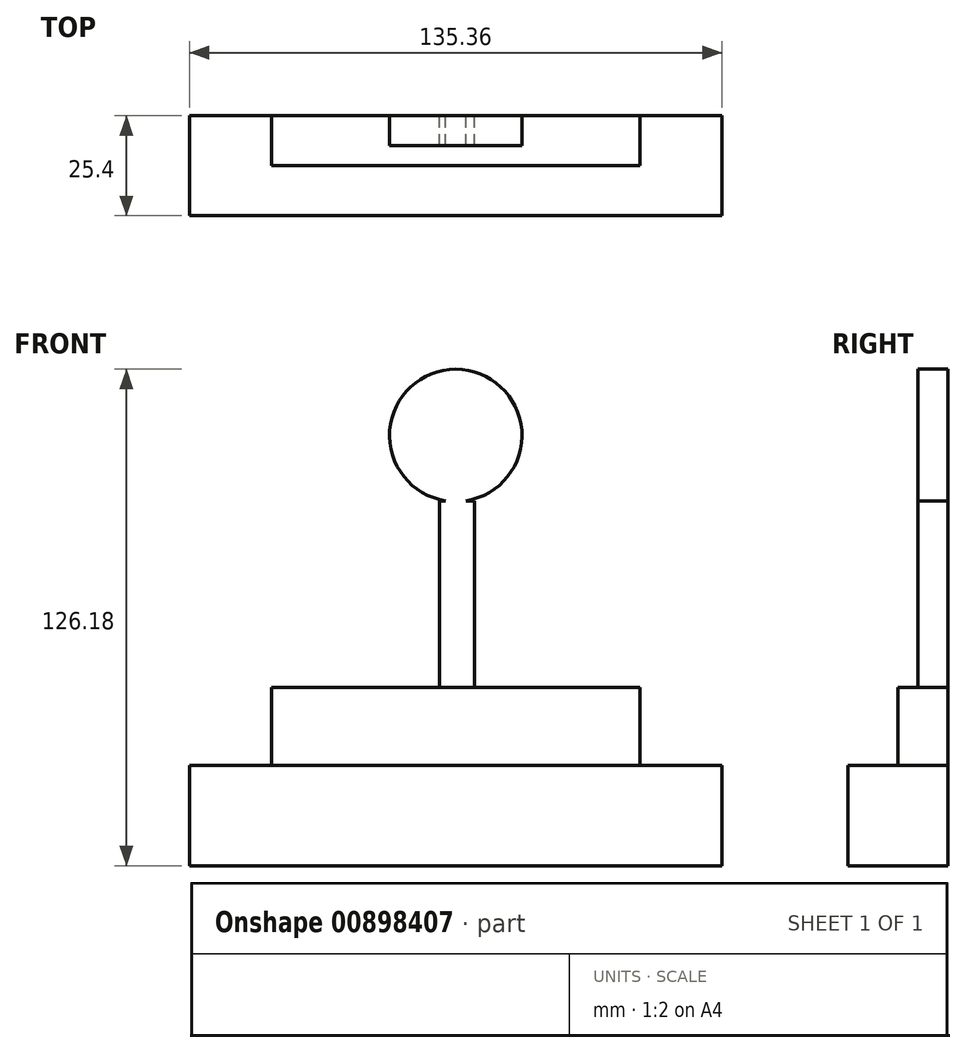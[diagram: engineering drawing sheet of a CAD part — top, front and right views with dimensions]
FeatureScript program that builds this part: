
annotation { "Feature Type Name" : "Feature", "Feature Type Description" : "" }
export const myFeature = defineFeature(function(context is Context, id is Id, definition is map)
    precondition{}
    {
        {
            var Q0;
            Q0=qCreatedBy(makeId("Front.planeOp"),FACE);
            var sketch = newSketch(context, id + "F0", { "sketchPlane" : qUnion([Q0])});
            skLineSegment(sketch, "E0.bottom", {"start": v(-67.68, -27.33) * mm, "end": v(67.68, -27.33) * mm});
            skLineSegment(sketch, "E0.top", {"start": v(-67.68, -52.83) * mm, "end": v(67.68, -52.83) * mm});
            skLineSegment(sketch, "E0.left", {"start": v(-67.68, -27.33) * mm, "end": v(-67.68, -52.83) * mm});
            skLineSegment(sketch, "E0.right", {"start": v(67.68, -27.33) * mm, "end": v(67.68, -52.83) * mm});
            skPoint(sketch, "E0.middle", {"position": v(0, -40.08) * mm});
            skLineSegment(sketch, "E1.bottom", {"start": v(-46.9, -7.35) * mm, "end": v(46.9, -7.35) * mm});
            skLineSegment(sketch, "E1.top", {"start": v(-46.9, -27.3) * mm, "end": v(46.9, -27.3) * mm});
            skLineSegment(sketch, "E1.left", {"start": v(-46.9, -7.35) * mm, "end": v(-46.9, -27.3) * mm});
            skLineSegment(sketch, "E1.right", {"start": v(46.9, -7.35) * mm, "end": v(46.9, -27.3) * mm});
            skPoint(sketch, "E1.middle", {"position": v(0, -17.33) * mm});
            skLineSegment(sketch, "E2.bottom", {"start": v(-5.61, 34.64) * mm, "end": v(4.92, 34.64) * mm});
            skLineSegment(sketch, "E2.top", {"start": v(-5.61, -7.35) * mm, "end": v(4.92, -7.35) * mm});
            skLineSegment(sketch, "E2.left", {"start": v(-5.61, 34.64) * mm, "end": v(-5.61, -7.35) * mm});
            skLineSegment(sketch, "E2.right", {"start": v(4.92, 34.64) * mm, "end": v(4.92, -7.35) * mm});
            skCircle(sketch, "E3", {"center": v(0, 53.45) * mm, "radius": 19.06 * mm});
            skLineSegment(sketch, "E4", {"start": v(0, 65.64) * mm, "end": v(-6.66, 55.94) * mm});
            skLineSegment(sketch, "E5", {"start": v(-6.66, 49) * mm, "end": v(-7.32, 41.58) * mm});
            skLineSegment(sketch, "E6", {"start": v(-7.32, 41.58) * mm, "end": v(0, 46.46) * mm});
            skLineSegment(sketch, "E7.MirrorCS", {"start": v(0, 65.64) * mm, "end": v(6.66, 55.94) * mm});
            skLineSegment(sketch, "E8.MirrorCS", {"start": v(7.32, 41.58) * mm, "end": v(0, 46.46) * mm});
            skLineSegment(sketch, "E9.MirrorCS", {"start": v(6.66, 49) * mm, "end": v(7.32, 41.58) * mm});
            skLineSegment(sketch, "E10", {"start": v(-6.66, 55.94) * mm, "end": v(-14.24, 55.94) * mm});
            skLineSegment(sketch, "E11", {"start": v(-14.24, 55.94) * mm, "end": v(-6.66, 49) * mm});
            skLineSegment(sketch, "E12", {"start": v(7.84, 55.94) * mm, "end": v(14.76, 55.94) * mm});
            skLineSegment(sketch, "E13", {"start": v(14.76, 55.94) * mm, "end": v(6.66, 49) * mm});
            skSolve(sketch);
        }
        {
            var Q0;
            Q0=makeQuery(id+"F0.imprint","IMPRINT",FACE,{"disambiguationData":[TD([[makeQuery(id+"F0.imprint","IMPRINT",EDGE,{"derivedFrom":sQuery(id+"F0.wireOp",EDGE,"E0.bottom")}),-1.0]])]});
            extrude(context, id + "F1", {"entities" : qUnion([Q0]), "depth" : 25.4 * mm, "offsetDistance" : 25.4 * mm});
        }
        {
            var Q0;
            Q0=qCreatedBy(makeId("Front.planeOp"),FACE);
            var sketch = newSketch(context, id + "F2", { "sketchPlane" : qUnion([Q0])});
            skLineSegment(sketch, "E14.bottom", {"start": v(-46.76, -27.43) * mm, "end": v(46.76, -27.43) * mm});
            skLineSegment(sketch, "E14.top", {"start": v(-46.76, -7.48) * mm, "end": v(46.76, -7.48) * mm});
            skLineSegment(sketch, "E14.left", {"start": v(-46.76, -27.43) * mm, "end": v(-46.76, -7.48) * mm});
            skLineSegment(sketch, "E14.right", {"start": v(46.76, -27.43) * mm, "end": v(46.76, -7.48) * mm});
            skPoint(sketch, "E15.middle", {"position": v(0, -17.46) * mm});
            skSolve(sketch);
        }
        {
            var Q0;
            Q0 = qSketchRegion(id + "F2", true);
            extrude(context, id + "F3", {"entities" : qUnion([Q0]), "operationType" : NewBodyOperationType.ADD, "depth" : 12.7 * mm, "offsetDistance" : 25.4 * mm});
        }
        {
            var Q0;
            Q0=qCreatedBy(makeId("Front.planeOp"),FACE);
            var sketch = newSketch(context, id + "F4", { "sketchPlane" : qUnion([Q0])});
            skLineSegment(sketch, "E16.top", {"start": v(0, -47.94) * mm, "end": v(0, -47.94) * mm});
            skPoint(sketch, "E16.middle", {"position": v(0, -1.94) * mm});
            skLineSegment(sketch, "E17.bottom", {"start": v(-4.09, -7.48) * mm, "end": v(4.78, -7.48) * mm});
            skLineSegment(sketch, "E17.top", {"start": v(-4.09, 39.9) * mm, "end": v(4.78, 39.9) * mm});
            skLineSegment(sketch, "E17.left", {"start": v(-4.09, -7.48) * mm, "end": v(-4.09, 39.9) * mm});
            skLineSegment(sketch, "E17.right", {"start": v(4.78, -7.48) * mm, "end": v(4.78, 39.9) * mm});
            skSolve(sketch);
        }
        {
            var Q0;
            Q0=makeQuery(id+"F4.imprint","IMPRINT",FACE,{"disambiguationData":[TD([[makeQuery(id+"F4.imprint","IMPRINT",EDGE,{"derivedFrom":sQuery(id+"F4.wireOp",EDGE,"E17.bottom")}),1.0]])]});
            extrude(context, id + "F5", {"entities" : qUnion([Q0]), "operationType" : NewBodyOperationType.ADD, "depth" : 7.62 * mm, "offsetDistance" : 25.4 * mm});
        }
        {
            var Q0;
            Q0=qCreatedBy(makeId("Front.planeOp"),FACE);
            var sketch = newSketch(context, id + "F6", { "sketchPlane" : qUnion([Q0])});
            skCircle(sketch, "E18", {"center": v(0, 56.53) * mm, "radius": 16.82 * mm});
            skSolve(sketch);
        }
        {
            var Q0;
            Q0=makeQuery(id+"F6.imprint","IMPRINT",FACE,{"disambiguationData":[TD([[makeQuery(id+"F6.imprint","IMPRINT",EDGE,{"derivedFrom":sQuery(id+"F6.wireOp",EDGE,"E18")}),1.0]])]});
            extrude(context, id + "F7", {"entities" : qUnion([Q0]), "operationType" : NewBodyOperationType.ADD, "depth" : 7.62 * mm, "offsetDistance" : 25.4 * mm});
        }
    });
